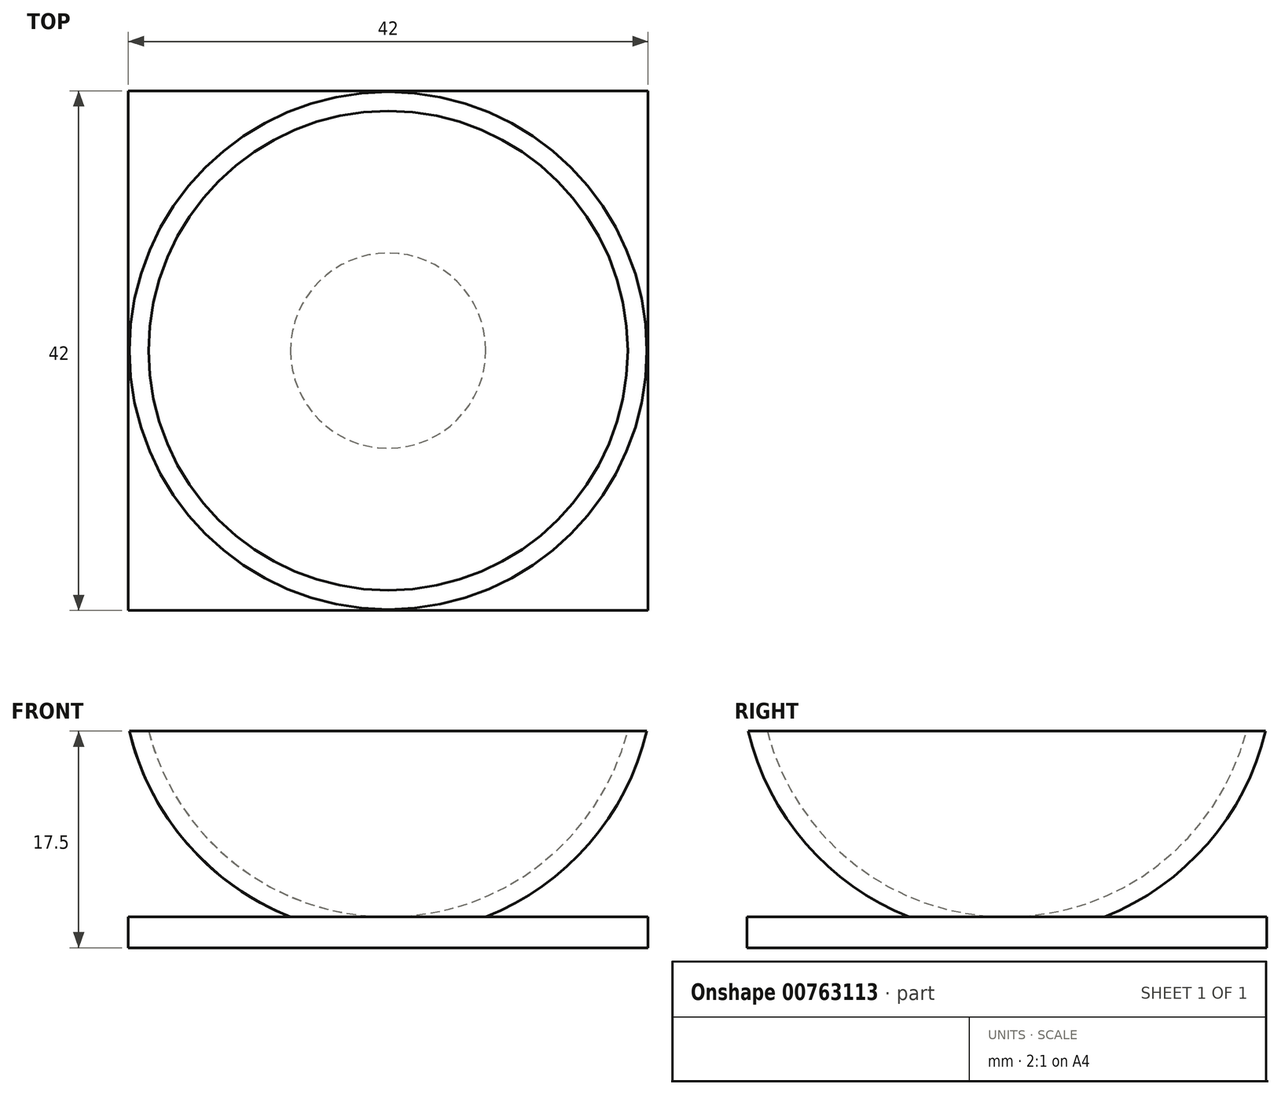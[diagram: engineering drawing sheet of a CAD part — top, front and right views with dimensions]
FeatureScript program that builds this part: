
annotation { "Feature Type Name" : "Feature", "Feature Type Description" : "" }
export const myFeature = defineFeature(function(context is Context, id is Id, definition is map)
    precondition{}
    {
        {
            var Q0;
            Q0=qCreatedBy(makeId("Top.planeOp"),FACE);
            var sketch = newSketch(context, id + "F0", { "sketchPlane" : qUnion([Q0])});
            skLineSegment(sketch, "E0.bottom", {"start": v(-21, 21) * mm, "end": v(21, 21) * mm});
            skLineSegment(sketch, "E0.top", {"start": v(-21, -21) * mm, "end": v(21, -21) * mm});
            skLineSegment(sketch, "E0.left", {"start": v(-21, 21) * mm, "end": v(-21, -21) * mm});
            skLineSegment(sketch, "E0.right", {"start": v(21, 21) * mm, "end": v(21, -21) * mm});
            skPoint(sketch, "E1", {"position": v(0, 21) * mm});
            skPoint(sketch, "E2", {"position": v(0, -21) * mm});
            skPoint(sketch, "E3", {"position": v(-21, 0) * mm});
            skPoint(sketch, "E4", {"position": v(21, 0) * mm});
            skLineSegment(sketch, "E5", {"start": v(0, 21) * mm, "end": v(0, -21) * mm, "construction": true});
            skLineSegment(sketch, "E6", {"start": v(-21, 0) * mm, "end": v(21, 0) * mm, "construction": true});
            skPoint(sketch, "E7", {"position": v(0, 0) * mm});
            skSolve(sketch);
        }
        {
            var Q0;
            Q0=qSketchRegion(id+"F0",true);
            extrude(context, id + "F1", {"entities" : qUnion([Q0]), "depth" : 2.5 * mm, "offsetDistance" : 25 * mm});
        }
        {
            var Q0;
            Q0=qCreatedBy(makeId("Front.planeOp"),FACE);
            var sketch = newSketch(context, id + "F2", { "sketchPlane" : qUnion([Q0])});
            skLineSegment(sketch, "E8", {"start": v(0, 0) * mm, "end": v(0, 17.5) * mm});
            skArc(sketch, "E9", {"start": v(-19.36, 17.5) * mm, "mid": v(0, 2.5) * mm, "end": v(19.36, 17.5) * mm});
            skArc(sketch, "E10", {"start": v(-20.91, 17.5) * mm, "mid": v(0, 1) * mm, "end": v(20.91, 17.5) * mm});
            skPoint(sketch, "E11", {"position": v(0, 17.5) * mm});
            skPoint(sketch, "E12", {"position": v(-19.36, 17.5) * mm});
            skPoint(sketch, "E13", {"position": v(-20.91, 17.5) * mm});
            skPoint(sketch, "E14", {"position": v(19.36, 17.5) * mm});
            skPoint(sketch, "E15", {"position": v(20.91, 17.5) * mm});
            skPoint(sketch, "E16.orphan", {"position": v(-21.5, 22.5) * mm});
            skPoint(sketch, "E17.orphan", {"position": v(-20, 22.5) * mm});
            skPoint(sketch, "E18.orphan", {"position": v(20, 22.5) * mm});
            skPoint(sketch, "E19.orphan", {"position": v(21.5, 22.5) * mm});
            skLineSegment(sketch, "E20", {"start": v(-20.91, 17.5) * mm, "end": v(-19.36, 17.5) * mm});
            skLineSegment(sketch, "E21", {"start": v(19.36, 17.5) * mm, "end": v(20.91, 17.5) * mm});
            skSolve(sketch);
        }
        {
            var Q0;
            {var subQ5=sQuery(id+"F2.wireOp",EDGE,"E20");Q0=makeQuery(id+"F2.imprint","IMPRINT",FACE,{"disambiguationData":[TD([[makeQuery(id+"F2.imprint","IMPRINT",EDGE,{"derivedFrom":subQ5}),-1.0]])]});}
            var Q1;
            Q1=sQuery(id+"F2.wireOp",EDGE,"E8");
            revolve(context, id + "F3", {"operationType" : NewBodyOperationType.ADD, "entities" : qUnion([Q0]), "axis" : qUnion([Q1]), "revolveType" : RevolveType.FULL});
        }
    });
